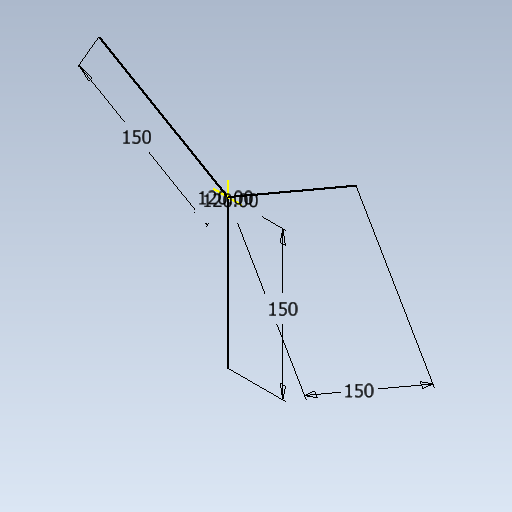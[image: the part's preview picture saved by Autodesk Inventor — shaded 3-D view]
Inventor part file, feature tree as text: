
AUTODESK INVENTOR PART (.ipt)
format: ipt  version: 2021 (Build 250183000, 183)  size: 102,400 bytes
history: native  units: mm
features: sketch x1
ambient origin geometry x8: Origin, YZ Plane, XZ Plane, XY Plane, X Axis, Y Axis, Z Axis, Center Point
feature tree (1):
  sketch  "Sketch6"  dims[d46=120.0deg d47=120.0deg d48=150.0mm d49=150.0mm d50=150.0mm]
